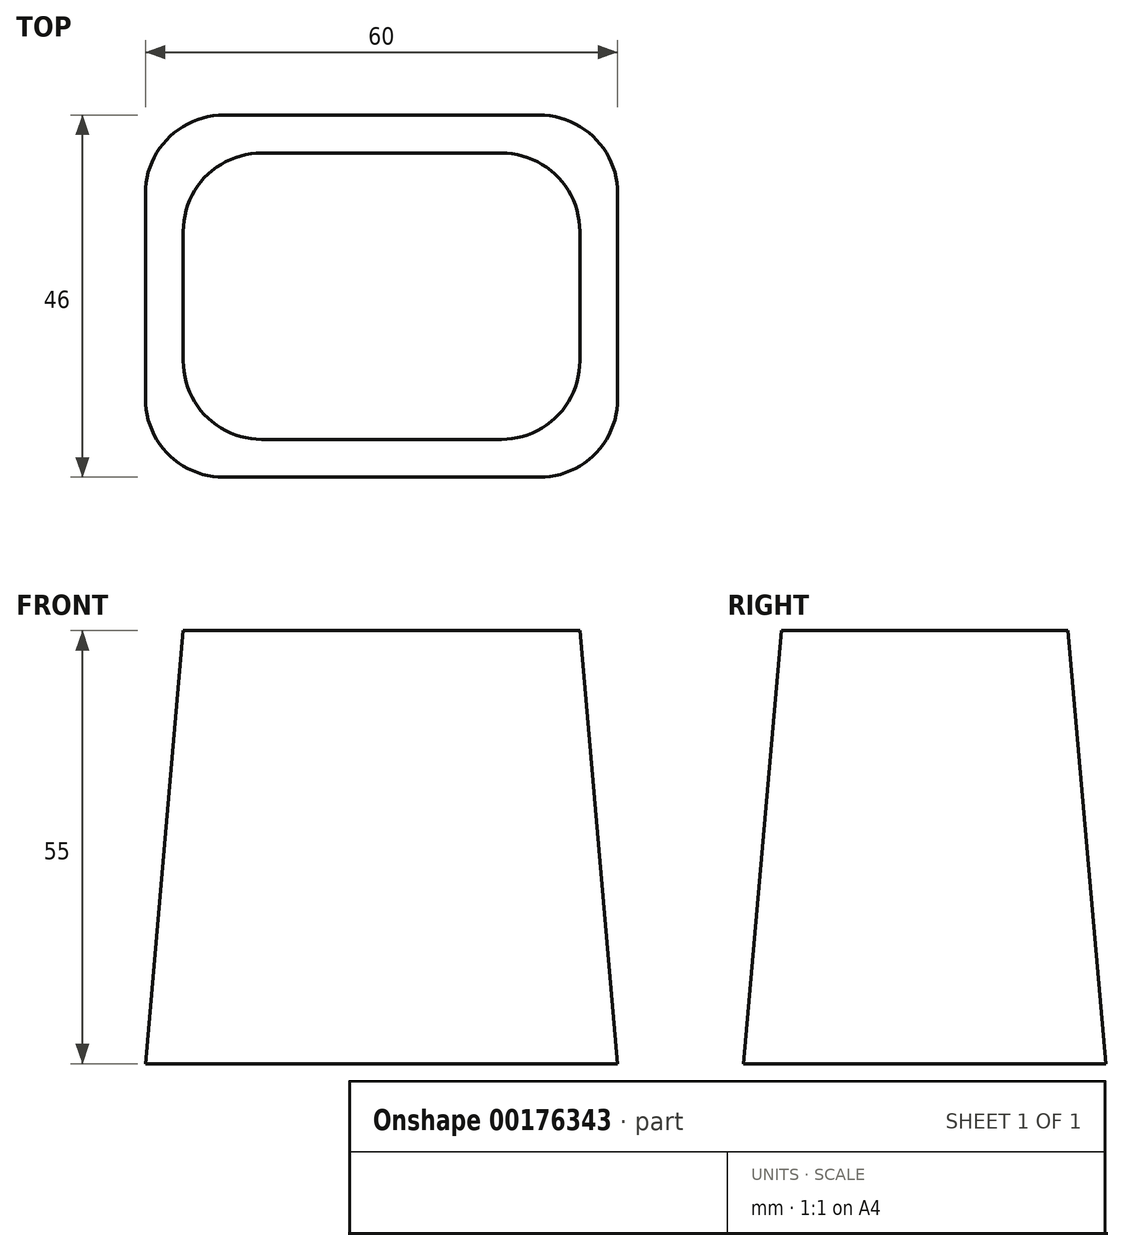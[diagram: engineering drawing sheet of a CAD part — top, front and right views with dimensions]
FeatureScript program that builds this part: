
annotation { "Feature Type Name" : "Feature", "Feature Type Description" : "" }
export const myFeature = defineFeature(function(context is Context, id is Id, definition is map)
    precondition{}
    {
        {
            var Q0;
            Q0=qCreatedBy(makeId("Top.planeOp"),FACE);
            var sketch = newSketch(context, id + "F0", { "sketchPlane" : qUnion([Q0])});
            skLineSegment(sketch, "E0.bottom", {"start": v(-30, -23) * mm, "end": v(30, -23) * mm});
            skLineSegment(sketch, "E0.top", {"start": v(-30, 23) * mm, "end": v(30, 23) * mm});
            skLineSegment(sketch, "E0.left", {"start": v(-30, -23) * mm, "end": v(-30, 23) * mm});
            skLineSegment(sketch, "E0.right", {"start": v(30, -23) * mm, "end": v(30, 23) * mm});
            skSolve(sketch);
        }
        {
            var Q0;
            Q0=makeQuery(id+"F0.imprint","IMPRINT",FACE,{"disambiguationData":[TD([[makeQuery(id+"F0.imprint","IMPRINT",EDGE,{"derivedFrom":sQuery(id+"F0.wireOp",EDGE,"E0.bottom")}),1.0]])]});
            extrude(context, id + "F1", {"entities" : qUnion([Q0]), "depth" : 55 * mm, "hasDraft" : true, "draftAngle" : 5 * degree, "draftPullDirection" : true});
        }
        {
            var Q0;
            Q0=makeQuery(id+"F1.opExtrude","SWEPT_EDGE",EDGE,{"disambiguationData":[OSD([sQuery(id+"F0.wireOp",EDGE,"E0.bottom"),sQuery(id+"F0.wireOp",EDGE,"E0.left")])]});
            var Q1;
            Q1=makeQuery(id+"F1.opExtrude","SWEPT_EDGE",EDGE,{"disambiguationData":[OSD([sQuery(id+"F0.wireOp",EDGE,"E0.bottom"),sQuery(id+"F0.wireOp",EDGE,"E0.right")])]});
            var Q2;
            Q2=makeQuery(id+"F1.opExtrude","SWEPT_EDGE",EDGE,{"disambiguationData":[OSD([sQuery(id+"F0.wireOp",EDGE,"E0.top"),sQuery(id+"F0.wireOp",EDGE,"E0.left")])]});
            var Q3;
            Q3=makeQuery(id+"F1.opExtrude","SWEPT_EDGE",EDGE,{"disambiguationData":[OSD([sQuery(id+"F0.wireOp",EDGE,"E0.top"),sQuery(id+"F0.wireOp",EDGE,"E0.right")])]});
            fillet(context, id + "F2", {"entities" : qUnion([Q0, Q1, Q2, Q3]), "radius" : 10 * mm, "tangentPropagation" : true, "allowEdgeOverflow" : false});
        }
    });
